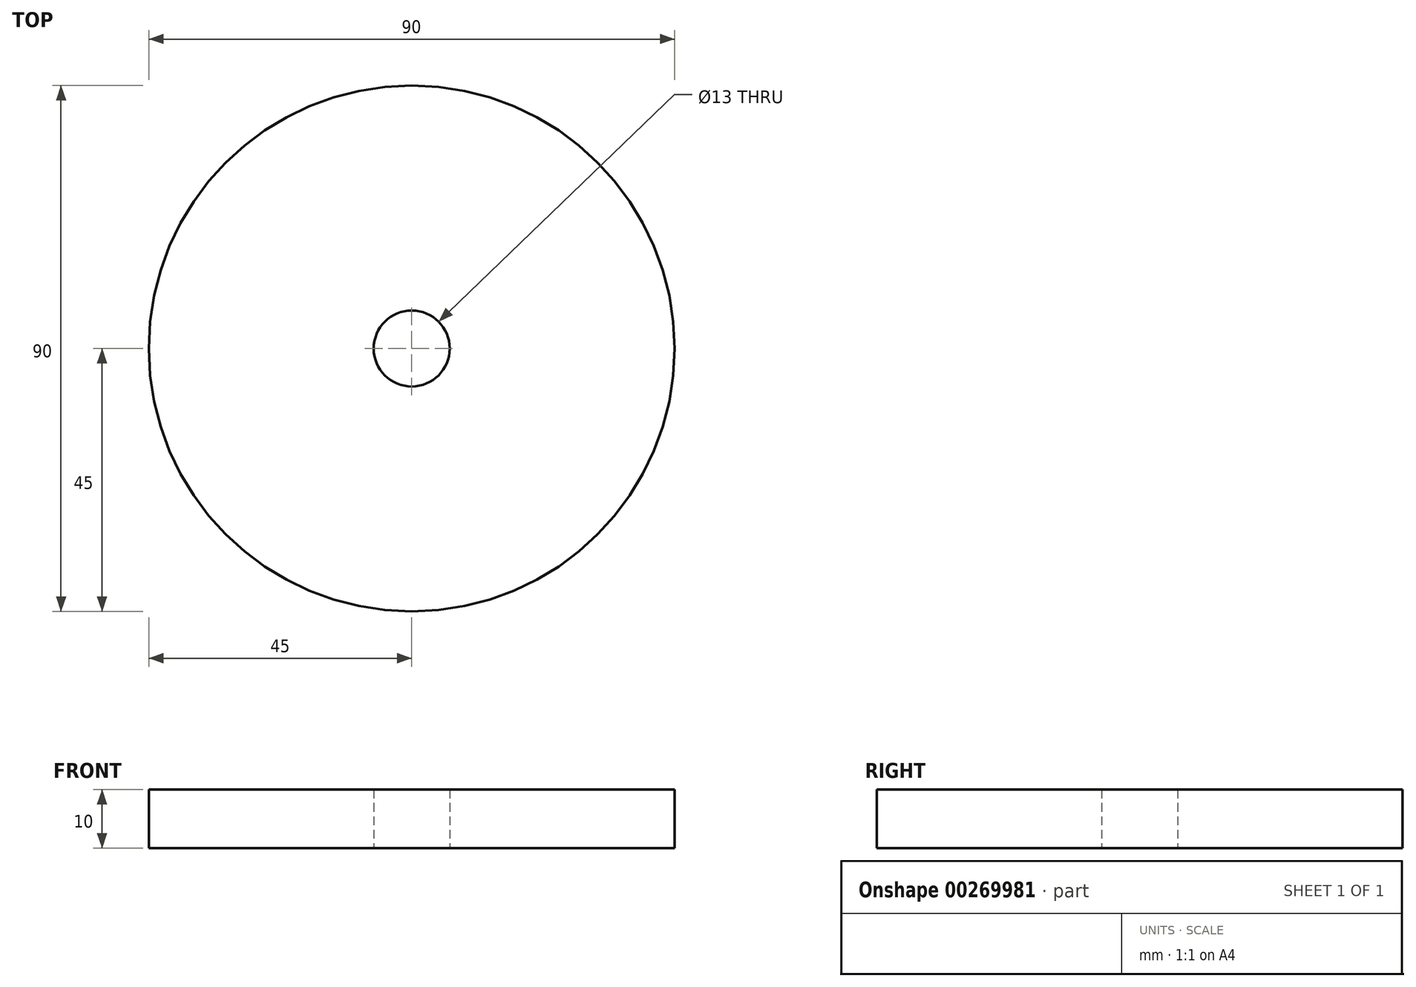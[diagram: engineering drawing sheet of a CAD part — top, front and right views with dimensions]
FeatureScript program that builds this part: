
annotation { "Feature Type Name" : "Feature", "Feature Type Description" : "" }
export const myFeature = defineFeature(function(context is Context, id is Id, definition is map)
    precondition{}
    {
        {
            var Q0;
            Q0=qCreatedBy(makeId("Top.planeOp"),FACE);
            var sketch = newSketch(context, id + "F0", { "sketchPlane" : qUnion([Q0])});
            skCircle(sketch, "E0", {"center": v(0, 0) * mm, "radius": 45 * mm});
            skCircle(sketch, "E1", {"center": v(0, 0) * mm, "radius": 6.5 * mm});
            skSolve(sketch);
        }
        {
            var Q0;
            Q0=makeQuery(id+"F0.imprint","IMPRINT",FACE,{"disambiguationData":[TD([[makeQuery(id+"F0.imprint","IMPRINT",EDGE,{"derivedFrom":sQuery(id+"F0.wireOp",EDGE,"E0")}),1.0]])]});
            extrude(context, id + "F1", {"entities" : qUnion([Q0]), "offsetDistance" : 25 * mm, "depth" : 10 * mm});
        }
    });
